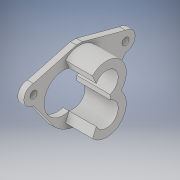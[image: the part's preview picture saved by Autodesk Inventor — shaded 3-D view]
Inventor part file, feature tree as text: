
AUTODESK INVENTOR PART (.ipt)
format: ipt  version: 2017 (Build 210142000, 142)  size: 168,960 bytes
history: native  units: in
note: dims shown in document units (in); Inventor stores cm internally (conversion verified against a paired STEP export)
features: extrude x2, sketch x2, chamfer x1, projected_geometry x1
ambient origin geometry x8: Origin, YZ Plane, XZ Plane, XY Plane, X Axis, Y Axis, Z Axis, Center Point
bodies: Solid1 (feature_tree)
feature tree (6):
  extrude  "Extrusion1"  Depth=0.2756in
  extrude  "Extrusion4"  Depth=0.2756in
  chamfer  "Chamfer1"  Distance=1.4567in
  sketch  "Sketch1"  dims[d0=0.475in d1=0.2756in]
  sketch  "Sketch4"  dims[d2=0.475in d3=0.2756in d5=1.4567in d6=0.8in d7=0.3285in d8=0.146in d11=0.146in d14=0.396in d15=0.396in d26=0.4002in d27=0.125in d28=0.0in d39=0.81in d40=0.81in d41=0.557in d42=0.0in d43=0.0625in d44=0.125in d45=45.0deg]
  projected_geometry  "Projected Loop3"
